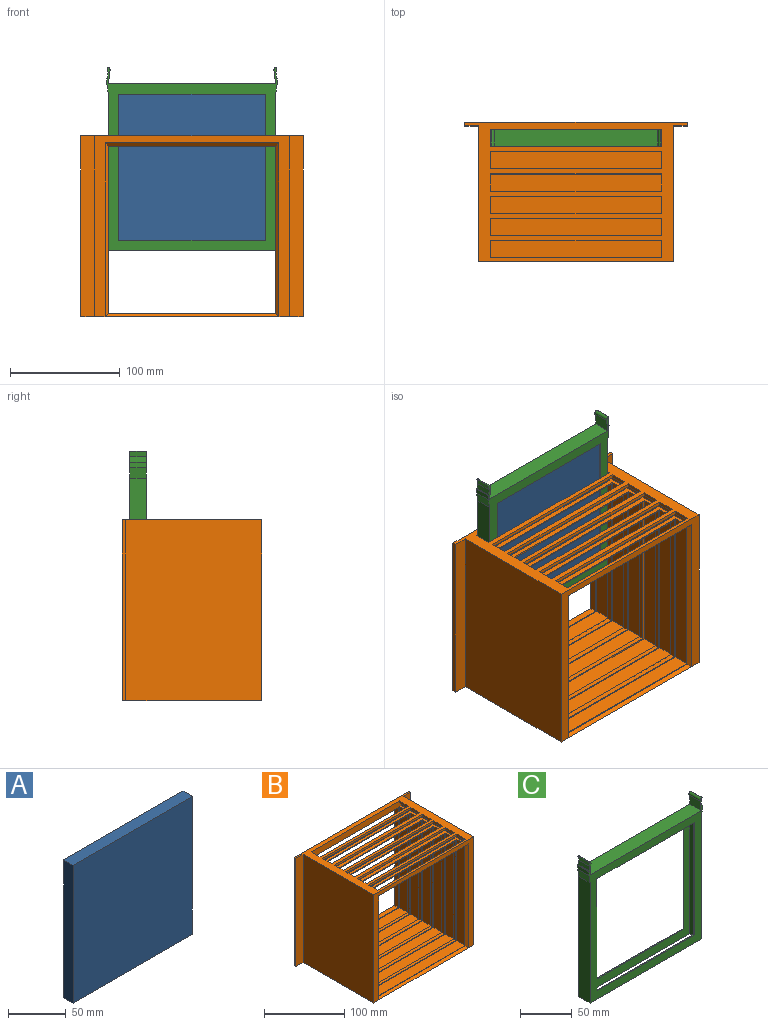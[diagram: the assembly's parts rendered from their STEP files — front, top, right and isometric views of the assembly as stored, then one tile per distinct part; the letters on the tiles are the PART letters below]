
ASSEMBLY  parts=3 mates=2
PART A: 6 faces, bbox 146.1x11.4x146.1 mm
  f0: plane 146.05x11.43mm, normal (-1,0,0), area 1669.4mm2, adj f1,f3,f4,f5
  f1: plane 146.05x11.43mm, normal (0,0,-1), area 1669.4mm2, adj f0,f2,f4,f5
  f2: plane 146.05x11.43mm, normal (1,0,0), area 1669.4mm2, adj f1,f3,f4,f5
  f3: plane 146.05x11.43mm, normal (0,0,1), area 1669.4mm2, adj f0,f2,f4,f5
  f4: plane 146.05x146.05mm, normal (0,-1,0), area 21330.6mm2, adj f0,f1,f2,f3
  f5: plane 146.05x146.05mm, normal (0,1,0), area 21330.6mm2, adj f0,f1,f2,f3
PART B: 94 faces, bbox 203.2x127x165.1 mm
  f0: plane 155.58x154.33mm, normal (0,-1,0), area 783.5mm2, adj f34,f36,f38,f39,f40,f41,f42,f90
  f1: plane 154.33x15.88mm, normal (-1,0,0), area 2449.9mm2, adj f2,f4,f47,f90
  f2: plane 155.58x154.33mm, normal (0,-1,0), area 783.5mm2, adj f1,f3,f47,f48,f49,f50,f51,f90
  f3: plane 154.33x15.88mm, normal (1,0,0), area 2449.9mm2, adj f2,f4,f47,f90
  f4: plane 155.58x154.33mm, normal (0,1,0), area 783.5mm2, adj f1,f3,f39,f40,f41,f42,f47,f90
  f5: plane 154.33x15.88mm, normal (-1,0,0), area 2449.9mm2, adj f6,f8,f56,f90
  f6: plane 155.58x154.33mm, normal (0,-1,0), area 783.5mm2, adj f5,f7,f56,f57,f58,f59,f60,f90
  f7: plane 154.33x15.88mm, normal (1,0,0), area 2449.9mm2, adj f6,f8,f56,f90
  f8: plane 155.58x154.33mm, normal (0,1,0), area 783.5mm2, adj f5,f7,f48,f49,f50,f51,f56,f90
  f9: plane 154.33x15.88mm, normal (-1,0,0), area 2449.9mm2, adj f10,f12,f65,f90
  f10: plane 155.58x154.33mm, normal (0,-1,0), area 783.5mm2, adj f9,f11,f65,f66,f67,f68,f69,f90
  f11: plane 154.33x15.88mm, normal (1,0,0), area 2449.9mm2, adj f10,f12,f65,f90
  f12: plane 155.58x154.33mm, normal (0,1,0), area 783.5mm2, adj f9,f11,f57,f58,f59,f60,f65,f90
  f13: plane 154.33x15.88mm, normal (-1,0,0), area 2449.9mm2, adj f14,f16,f74,f90
  f14: plane 155.58x154.33mm, normal (0,-1,0), area 783.5mm2, adj f13,f15,f74,f75,f76,f77,f78,f90
  f15: plane 154.33x15.88mm, normal (1,0,0), area 2449.9mm2, adj f14,f16,f74,f90
  f16: plane 155.58x154.33mm, normal (0,1,0), area 783.5mm2, adj f13,f15,f66,f67,f68,f69,f74,f90
  f17: plane 154.33x15.88mm, normal (1,0,0), area 2449.9mm2, adj f18,f79,f83,f90
  f18: plane 155.58x154.33mm, normal (0,1,0), area 783.5mm2, adj f17,f19,f75,f76,f77,f78,f83,f90
  f19: plane 154.33x15.88mm, normal (-1,0,0), area 2449.9mm2, adj f18,f79,f83,f90
  f20: plane 203.2x127mm, normal (0,0,1), area 7842.7mm2, adj f25,f26,f27,f29,f30,f31,f32,f33
  f21: plane 152.4x6.35mm, normal (1,0,0), area 967.7mm2, adj f22,f24,f29,f79
  f22: plane 152.4x6.35mm, normal (0,0,1), area 967.7mm2, adj f21,f23,f29,f79
  f23: plane 152.4x6.35mm, normal (-1,0,0), area 967.7mm2, adj f22,f24,f29,f79
  f24: plane 152.4x6.35mm, normal (0,0,-1), area 967.7mm2, adj f21,f23,f29,f79
  f25: plane 177.8x165.1mm, normal (0,-1,0), area 4153.2mm2, adj f20,f28,f31,f33,f85,f86,f87
  f26: plane 165.1x3.18mm, normal (-1,0,0), area 524.2mm2, adj f20,f28,f29,f32
  f27: plane 165.1x3.18mm, normal (1,0,0), area 524.2mm2, adj f20,f28,f29,f30
  f28: plane 203.2x127mm, normal (0,0,-1), area 22661.2mm2, adj f25,f26,f27,f29,f30,f31,f32,f33
  f29: plane 203.2x165.1mm, normal (0,1,0), area 10322.6mm2, adj f20,f21,f22,f23,f24,f26,f27,f28
  f30: plane 165.1x12.7mm, normal (0,-1,0), area 2096.8mm2, adj f20,f27,f28,f31
  f31: plane 165.1x123.83mm, normal (1,0,0), area 20443.5mm2, adj f20,f25,f28,f30
  f32: plane 165.1x12.7mm, normal (0,-1,0), area 2096.8mm2, adj f20,f26,f28,f33
  f33: plane 165.1x123.83mm, normal (-1,0,0), area 20443.5mm2, adj f20,f25,f28,f32
  f34: plane 162.81x15.88mm, normal (-1,0,0), area 2510.6mm2, adj f0,f20,f35,f37,f38,f89,f90,f93
  f35: plane 155.58x3.09mm, normal (0,-1,0), area 480.1mm2, adj f20,f34,f36,f89
  f36: plane 162.81x15.88mm, normal (1,0,0), area 2510.6mm2, adj f0,f20,f35,f37,f38,f88,f89,f90
  f37: plane 162.81x155.58mm, normal (0,1,0), area 2104mm2, adj f20,f34,f36,f38,f84,f85,f86,f87
  f38: plane 155.58x15.88mm, normal (0,0,1), area 2469.8mm2, adj f0,f34,f36,f37
  f39: plane 152.4x4.45mm, normal (0,0,-1), area 677.4mm2, adj f0,f4,f40,f42
  f40: plane 152.4x4.45mm, normal (-1,0,0), area 677.4mm2, adj f0,f4,f39,f41
  f41: plane 152.4x4.45mm, normal (0,0,1), area 677.4mm2, adj f0,f4,f40,f42
  f42: plane 152.4x4.45mm, normal (1,0,0), area 677.4mm2, adj f0,f4,f39,f41
  f43: plane 15.88x3.09mm, normal (-1,0,0), area 49mm2, adj f20,f44,f46,f89
  f44: plane 155.58x3.09mm, normal (0,-1,0), area 480.1mm2, adj f20,f43,f45,f89
  f45: plane 15.88x3.09mm, normal (1,0,0), area 49mm2, adj f20,f44,f46,f89
  f46: plane 155.58x3.09mm, normal (0,1,0), area 480.1mm2, adj f20,f43,f45,f89
  f47: plane 155.58x15.88mm, normal (0,0,1), area 2469.8mm2, adj f1,f2,f3,f4
  f48: plane 152.4x4.45mm, normal (0,0,-1), area 677.4mm2, adj f2,f8,f49,f51
  f49: plane 152.4x4.45mm, normal (-1,0,0), area 677.4mm2, adj f2,f8,f48,f50
  f50: plane 152.4x4.45mm, normal (0,0,1), area 677.4mm2, adj f2,f8,f49,f51
  f51: plane 152.4x4.45mm, normal (1,0,0), area 677.4mm2, adj f2,f8,f48,f50
  f52: plane 15.88x3.09mm, normal (-1,0,0), area 49mm2, adj f20,f53,f55,f89
  f53: plane 155.58x3.09mm, normal (0,-1,0), area 480.1mm2, adj f20,f52,f54,f89
  f54: plane 15.88x3.09mm, normal (1,0,0), area 49mm2, adj f20,f53,f55,f89
  f55: plane 155.58x3.09mm, normal (0,1,0), area 480.1mm2, adj f20,f52,f54,f89
  f56: plane 155.58x15.88mm, normal (0,0,1), area 2469.8mm2, adj f5,f6,f7,f8
  f57: plane 152.4x4.45mm, normal (0,0,-1), area 677.4mm2, adj f6,f12,f58,f60
  f58: plane 152.4x4.45mm, normal (-1,0,0), area 677.4mm2, adj f6,f12,f57,f59
  f59: plane 152.4x4.45mm, normal (0,0,1), area 677.4mm2, adj f6,f12,f58,f60
  f60: plane 152.4x4.45mm, normal (1,0,0), area 677.4mm2, adj f6,f12,f57,f59
  f61: plane 15.88x3.09mm, normal (-1,0,0), area 49mm2, adj f20,f62,f64,f89
  f62: plane 155.58x3.09mm, normal (0,-1,0), area 480.1mm2, adj f20,f61,f63,f89
  f63: plane 15.88x3.09mm, normal (1,0,0), area 49mm2, adj f20,f62,f64,f89
  f64: plane 155.58x3.09mm, normal (0,1,0), area 480.1mm2, adj f20,f61,f63,f89
  f65: plane 155.58x15.88mm, normal (0,0,1), area 2469.8mm2, adj f9,f10,f11,f12
  f66: plane 152.4x4.45mm, normal (0,0,-1), area 677.4mm2, adj f10,f16,f67,f69
  f67: plane 152.4x4.45mm, normal (-1,0,0), area 677.4mm2, adj f10,f16,f66,f68
  f68: plane 152.4x4.45mm, normal (0,0,1), area 677.4mm2, adj f10,f16,f67,f69
  f69: plane 152.4x4.45mm, normal (1,0,0), area 677.4mm2, adj f10,f16,f66,f68
  f70: plane 15.88x3.09mm, normal (-1,0,0), area 49mm2, adj f20,f71,f73,f89
  f71: plane 155.58x3.09mm, normal (0,-1,0), area 480.1mm2, adj f20,f70,f72,f89
  f72: plane 15.88x3.09mm, normal (1,0,0), area 49mm2, adj f20,f71,f73,f89
  f73: plane 155.58x3.09mm, normal (0,1,0), area 480.1mm2, adj f20,f70,f72,f89
  f74: plane 155.58x15.88mm, normal (0,0,1), area 2469.8mm2, adj f13,f14,f15,f16
  f75: plane 152.4x4.45mm, normal (0,0,-1), area 677.4mm2, adj f14,f18,f76,f78
  f76: plane 152.4x4.45mm, normal (-1,0,0), area 677.4mm2, adj f14,f18,f75,f77
  f77: plane 152.4x4.45mm, normal (0,0,1), area 677.4mm2, adj f14,f18,f76,f78
  f78: plane 152.4x4.45mm, normal (1,0,0), area 677.4mm2, adj f14,f18,f75,f77
  f79: plane 162.81x160.93mm, normal (0,-1,0), area 2132.9mm2, adj f17,f19,f20,f21,f22,f23,f24,f80
  f80: plane 15.88x3.09mm, normal (1,0,0), area 49mm2, adj f20,f79,f81,f89
  f81: plane 155.58x3.09mm, normal (0,1,0), area 480.1mm2, adj f20,f80,f82,f89
  f82: plane 15.88x3.09mm, normal (-1,0,0), area 49mm2, adj f20,f79,f81,f89
  f83: plane 155.58x15.88mm, normal (0,0,1), area 2469.8mm2, adj f17,f18,f19,f79
  f84: plane 158.75x3.18mm, normal (0,-0.71,0.71), area 698.6mm2, adj f28,f37,f85,f86
  f85: plane 158.75x3.18mm, normal (0.71,-0.71,0), area 698.6mm2, adj f25,f37,f84,f87
  f86: plane 158.75x3.18mm, normal (-0.71,-0.71,0), area 698.6mm2, adj f25,f37,f84,f87
  f87: plane 158.75x3.18mm, normal (0,-0.71,-0.71), area 698.6mm2, adj f25,f37,f85,f86
  f88: plane 5.4x2.32mm, normal (0,1,0), area 12.6mm2, adj f36,f89,f90,f91
  f89: plane 160.93x115.32mm, normal (0,0,-1), area 4075.1mm2, adj f34,f35,f36,f43,f44,f45,f46,f52
  f90: plane 160.93x115.32mm, normal (0,0,1), area 4075.1mm2, adj f0,f1,f2,f3,f4,f5,f6,f7
  f91: plane 115.32x5.4mm, normal (1,0,0), area 622.9mm2, adj f79,f88,f89,f90
  f92: plane 115.32x5.4mm, normal (-1,0,0), area 622.9mm2, adj f79,f89,f90,f93
  f93: plane 5.4x3.03mm, normal (0,1,0), area 16.4mm2, adj f34,f89,f90,f92
PART C: 37 faces, bbox 156x15.2x167.5 mm
  f0: plane 167.49x156mm, normal (0,-1,0), area 5514.8mm2, adj f4,f5,f6,f7,f11,f12,f13,f14
  f1: plane 167.49x156mm, normal (0,1,0), area 5514.8mm2, adj f4,f5,f6,f7,f15,f16,f17,f18
  f2: plane 147.32x146.05mm, normal (0,-1,0), area 3733.9mm2, adj f4,f8,f9,f10,f15,f16,f17,f18
  f3: plane 147.32x146.05mm, normal (0,1,0), area 3733.9mm2, adj f4,f8,f9,f10,f11,f12,f13,f14
  f4: plane 152.4x15.24mm, normal (0,0,-1), area 451.6mm2, adj f0,f1,f2,f3,f5,f6,f8,f9
  f5: plane 142.88x15.24mm, normal (-1,0,0), area 2177.4mm2, adj f0,f1,f4,f36
  f6: plane 142.88x15.24mm, normal (1,0,0), area 2177.4mm2, adj f0,f1,f4,f19
  f7: plane 152.4x15.24mm, normal (0,0,1), area 2322.6mm2, adj f0,f1,f27,f28
  f8: plane 146.05x12.7mm, normal (1,0,0), area 1854.8mm2, adj f2,f3,f4,f10
  f9: plane 146.05x12.7mm, normal (-1,0,0), area 1854.8mm2, adj f2,f3,f4,f10
  f10: plane 147.32x12.7mm, normal (0,0,-1), area 1871mm2, adj f2,f3,f8,f9
  f11: plane 133.35x1.27mm, normal (0,0,-1), area 169.4mm2, adj f0,f3,f12,f14
  f12: plane 133.35x1.27mm, normal (-1,0,0), area 169.4mm2, adj f0,f3,f11,f13
  f13: plane 133.35x1.27mm, normal (0,0,1), area 169.4mm2, adj f0,f3,f12,f14
  f14: plane 133.35x1.27mm, normal (1,0,0), area 169.4mm2, adj f0,f3,f11,f13
  f15: plane 133.35x1.27mm, normal (1,0,0), area 169.4mm2, adj f1,f2,f16,f18
  f16: plane 133.35x1.27mm, normal (0,0,1), area 169.4mm2, adj f1,f2,f15,f17
  f17: plane 133.35x1.27mm, normal (-1,0,0), area 169.4mm2, adj f1,f2,f16,f18
  f18: plane 133.35x1.27mm, normal (0,0,-1), area 169.4mm2, adj f1,f2,f15,f17
  f19: plane 15.24x9.53mm, normal (0.99,0,-0.16), area 147.1mm2, adj f0,f1,f6,f20
  f20: plane 15.24x4.5mm, normal (1,0,0), area 68.5mm2, adj f0,f1,f19,f21
  f21: plane 15.24x0.58mm, normal (0.92,0,-0.4), area 9.7mm2, adj f0,f1,f20,f22
  f22: plane 15.24x0.51mm, normal (0,0,1), area 7.7mm2, adj f0,f1,f21,f23
  f23: plane 15.24x5mm, normal (0.98,0,0.17), area 77.4mm2, adj f0,f1,f22,f24
  f24: plane 15.24x5mm, normal (0.98,0,-0.17), area 77.4mm2, adj f0,f1,f23,f25
  f25: plane 15.24x0.24mm, normal (0,0,1), area 3.7mm2, adj f0,f1,f24,f26
  f26: cylinder r=2.54mm len=15.24mm, axis (0,-1,0), area 65.4mm2, adj f0,f1,f25,f27
  f27: plane 15.24x12.24mm, normal (-0.99,0,-0.12), area 187.9mm2, adj f0,f1,f7,f26
  f28: plane 15.24x12.24mm, normal (0.99,0,-0.12), area 187.9mm2, adj f0,f1,f7,f29
  f29: cylinder r=2.54mm len=15.24mm, axis (0,-1,0), area 65.4mm2, adj f0,f1,f28,f30
  f30: plane 15.24x0.24mm, normal (0,0,1), area 3.7mm2, adj f0,f1,f29,f31
  f31: plane 15.24x5mm, normal (-0.98,0,-0.17), area 77.4mm2, adj f0,f1,f30,f32
  f32: plane 15.24x5mm, normal (-0.98,0,0.17), area 77.4mm2, adj f0,f1,f31,f33
  f33: plane 15.24x0.51mm, normal (0,0,1), area 7.7mm2, adj f0,f1,f32,f34
  f34: plane 15.24x0.58mm, normal (-0.92,0,-0.4), area 9.7mm2, adj f0,f1,f33,f35
  f35: plane 15.24x4.5mm, normal (-1,0,0), area 68.5mm2, adj f0,f1,f34,f36
  f36: plane 15.24x9.53mm, normal (-0.99,0,-0.16), area 147.1mm2, adj f0,f1,f5,f35
PLACE A t=(29.32,-8.57,60.2)mm
PLACE B at identity
PLACE C t=(25.4,-21.91,60.2)mm
MATE slider C.f7 <-> B.f83  axis (0,0,1) through (101.6,-14.29,212.6)mm
MATE fastened A.f3 <-> C.f10  axis (0,0,1) through (102.34,-14.29,206.25)mm
